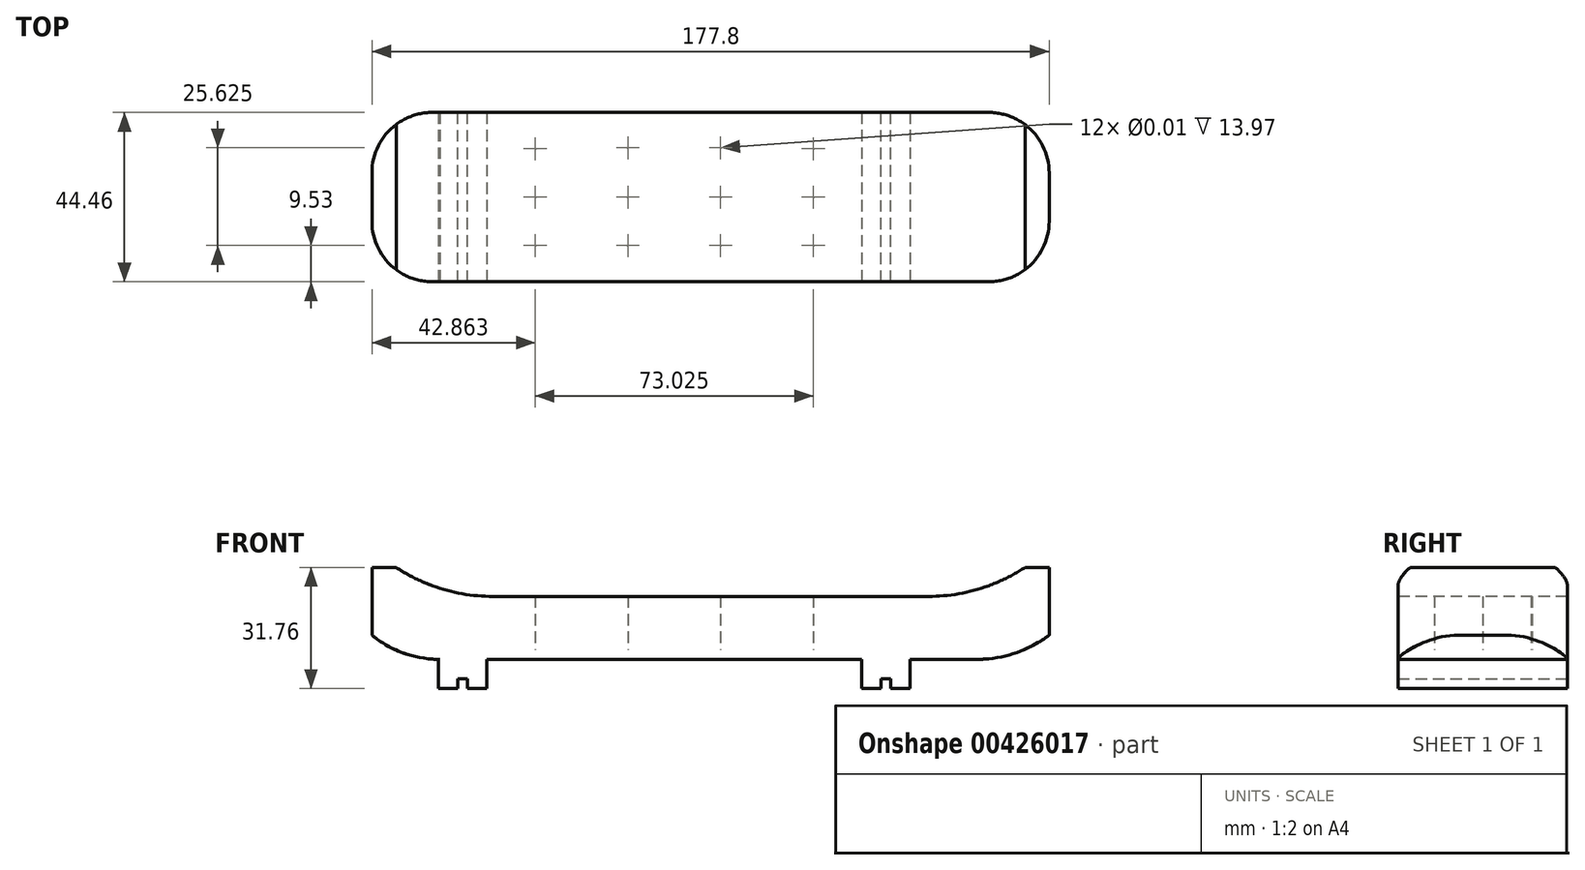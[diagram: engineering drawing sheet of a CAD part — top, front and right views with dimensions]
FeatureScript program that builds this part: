
annotation { "Feature Type Name" : "Feature", "Feature Type Description" : "" }
export const myFeature = defineFeature(function(context is Context, id is Id, definition is map)
    precondition{}
    {
        {
            var Q0;
            Q0=qCreatedBy(makeId("Front.planeOp"),FACE);
            var sketch = newSketch(context, id + "F0", { "sketchPlane" : qUnion([Q0])});
            skLineSegment(sketch, "E0.bottom", {"start": v(-88.9, -15.88) * mm, "end": v(88.9, -15.88) * mm});
            skLineSegment(sketch, "E0.top", {"start": v(-88.9, 15.88) * mm, "end": v(88.9, 15.88) * mm});
            skLineSegment(sketch, "E0.left", {"start": v(-88.9, -15.88) * mm, "end": v(-88.9, 15.88) * mm});
            skLineSegment(sketch, "E0.right", {"start": v(88.9, -15.88) * mm, "end": v(88.9, 15.88) * mm});
            skLineSegment(sketch, "E1", {"start": v(-88.9, 15.88) * mm, "end": v(88.9, -15.88) * mm, "construction": true});
            skPoint(sketch, "E2", {"position": v(0, 0) * mm});
            skSolve(sketch);
        }
        {
            var Q0;
            Q0=makeQuery(id+"F0.imprint","IMPRINT",FACE,{"disambiguationData":[TD([[makeQuery(id+"F0.imprint","IMPRINT",EDGE,{"derivedFrom":sQuery(id+"F0.wireOp",EDGE,"E0.bottom")}),1.0]])]});
            extrude(context, id + "F12", {"entities" : qUnion([Q0]), "endBound" : BoundingType.SYMMETRIC, "depth" : 44.45 * mm});
        }
        {
            var Q0;
            Q0=qCreatedBy(makeId("Front.planeOp"),FACE);
            var sketch = newSketch(context, id + "F1", { "sketchPlane" : qUnion([Q0])});
            skLineSegment(sketch, "E3.0", {"start": v(-88.9, -15.88) * mm, "end": v(88.9, -15.88) * mm, "construction": true});
            skLineSegment(sketch, "E4.bottom", {"start": v(-66.36, -15.88) * mm, "end": v(-63.82, -15.88) * mm});
            skLineSegment(sketch, "E4.top", {"start": v(-66.36, -13.34) * mm, "end": v(-63.82, -13.34) * mm});
            skLineSegment(sketch, "E4.left", {"start": v(-66.36, -15.88) * mm, "end": v(-66.36, -13.34) * mm});
            skLineSegment(sketch, "E4.right", {"start": v(-63.82, -15.88) * mm, "end": v(-63.82, -13.34) * mm});
            skLineSegment(sketch, "E5.bottom", {"start": v(44.77, -15.88) * mm, "end": v(47.3, -15.88) * mm});
            skLineSegment(sketch, "E5.top", {"start": v(44.77, -13.34) * mm, "end": v(47.3, -13.34) * mm});
            skLineSegment(sketch, "E5.left", {"start": v(44.77, -15.88) * mm, "end": v(44.77, -13.34) * mm});
            skLineSegment(sketch, "E5.right", {"start": v(47.3, -15.88) * mm, "end": v(47.3, -13.34) * mm});
            skPoint(sketch, "E6", {"position": v(-65.09, -15.88) * mm});
            skPoint(sketch, "E7", {"position": v(46.04, -15.88) * mm});
            skSolve(sketch);
        }
        {
            var Q0;
            Q0=qSketchRegion(id+"F1",true);
            extrude(context, id + "F2", {"entities" : qUnion([Q0]), "operationType" : NewBodyOperationType.REMOVE, "endBound" : BoundingType.UP_TO_NEXT, "depth" : 50.8 * mm, "hasSecondDirection" : true, "secondDirectionBound" : SecondDirectionBoundingType.UP_TO_NEXT, "secondDirectionOppositeDirection" : true, "secondDirectionDepth" : 25.4 * mm});
        }
        {
            var Q0;
            Q0=makeQuery(id+"F12.opExtrude","CAP_FACE",FACE,{"disambiguationData":[OSD([sQuery(id+"F0.wireOp",EDGE,"E0.bottom"),sQuery(id+"F0.wireOp",EDGE,"E0.top"),sQuery(id+"F0.wireOp",EDGE,"E0.left"),sQuery(id+"F0.wireOp",EDGE,"E0.right")])],"isStart":false});
            var sketch = newSketch(context, id + "F3", { "sketchPlane" : qUnion([Q0])});
            skLineSegment(sketch, "E8.bottom", {"start": v(-88.9, -15.88) * mm, "end": v(-71.44, -15.88) * mm});
            skLineSegment(sketch, "E8.top", {"start": v(-88.9, -8.26) * mm, "end": v(-71.44, -8.26) * mm});
            skLineSegment(sketch, "E8.left", {"start": v(-88.9, -15.88) * mm, "end": v(-88.9, -8.26) * mm});
            skLineSegment(sketch, "E8.right", {"start": v(-71.44, -15.88) * mm, "end": v(-71.44, -8.26) * mm});
            skLineSegment(sketch, "E9.bottom", {"start": v(-58.74, -15.88) * mm, "end": v(39.69, -15.88) * mm});
            skLineSegment(sketch, "E9.top", {"start": v(-58.74, -8.26) * mm, "end": v(39.69, -8.26) * mm});
            skLineSegment(sketch, "E9.left", {"start": v(-58.74, -15.88) * mm, "end": v(-58.74, -8.26) * mm});
            skLineSegment(sketch, "E9.right", {"start": v(39.69, -15.88) * mm, "end": v(39.69, -8.26) * mm});
            skLineSegment(sketch, "E10.bottom", {"start": v(88.9, -15.88) * mm, "end": v(52.39, -15.88) * mm});
            skLineSegment(sketch, "E10.top", {"start": v(88.9, -8.26) * mm, "end": v(52.39, -8.26) * mm});
            skLineSegment(sketch, "E10.left", {"start": v(88.9, -15.88) * mm, "end": v(88.9, -8.26) * mm});
            skLineSegment(sketch, "E10.right", {"start": v(52.39, -15.88) * mm, "end": v(52.39, -8.26) * mm});
            skLineSegment(sketch, "E11", {"start": v(39.69, -8.26) * mm, "end": v(52.39, -8.26) * mm, "construction": true});
            skPoint(sketch, "E12", {"position": v(46.04, -8.26) * mm});
            skPoint(sketch, "E13", {"position": v(46.04, -13.34) * mm});
            skLineSegment(sketch, "E14", {"start": v(-71.44, -8.26) * mm, "end": v(-58.74, -8.26) * mm, "construction": true});
            skPoint(sketch, "E15", {"position": v(-65.09, -8.26) * mm});
            skPoint(sketch, "E16", {"position": v(-65.09, -13.34) * mm});
            skSolve(sketch);
        }
        {
            var Q0;
            Q0=makeQuery(id+"F3.imprint","IMPRINT",FACE,{"disambiguationData":[TD([[makeQuery(id+"F3.imprint","IMPRINT",EDGE,{"derivedFrom":sQuery(id+"F3.wireOp",EDGE,"E8.bottom")}),1.0]])]});
            var Q1;
            Q1=makeQuery(id+"F3.imprint","IMPRINT",FACE,{"disambiguationData":[TD([[makeQuery(id+"F3.imprint","IMPRINT",EDGE,{"derivedFrom":sQuery(id+"F3.wireOp",EDGE,"E9.bottom")}),1.0]])]});
            var Q2;
            Q2=makeQuery(id+"F3.imprint","IMPRINT",FACE,{"disambiguationData":[TD([[makeQuery(id+"F3.imprint","IMPRINT",EDGE,{"derivedFrom":sQuery(id+"F3.wireOp",EDGE,"E10.bottom")}),1.0]])]});
            extrude(context, id + "F4", {"entities" : qUnion([Q0, Q1, Q2]), "operationType" : NewBodyOperationType.REMOVE, "endBound" : BoundingType.THROUGH_ALL, "oppositeDirection" : true, "depth" : 25.4 * mm});
        }
        {
            var Q0;
            Q0=makeQuery(id+"F12.opExtrude","CAP_FACE",FACE,{"disambiguationData":[OSD([sQuery(id+"F0.wireOp",EDGE,"E0.bottom"),sQuery(id+"F0.wireOp",EDGE,"E0.top"),sQuery(id+"F0.wireOp",EDGE,"E0.left"),sQuery(id+"F0.wireOp",EDGE,"E0.right")])],"isStart":false});
            var sketch = newSketch(context, id + "F5", { "sketchPlane" : qUnion([Q0])});
            skArc(sketch, "E17", {"start": v(-88.9, -1.9) * mm, "mid": v(-80.56, -6.62) * mm, "end": v(-71.12, -8.26) * mm});
            skLineSegment(sketch, "E18", {"start": v(-71.12, -8.26) * mm, "end": v(-88.9, -8.26) * mm});
            skLineSegment(sketch, "E19", {"start": v(-88.9, -8.26) * mm, "end": v(-88.9, -1.9) * mm});
            skArc(sketch, "E20", {"start": v(-82.55, 15.87) * mm, "mid": v(-70.4, 10.2) * mm, "end": v(-57.15, 8.25) * mm});
            skLineSegment(sketch, "E21", {"start": v(-57.15, 8.26) * mm, "end": v(57.15, 8.26) * mm});
            skArc(sketch, "E22", {"start": v(57.15, 8.26) * mm, "mid": v(70.4, 10.2) * mm, "end": v(82.55, 15.88) * mm});
            skLineSegment(sketch, "E23", {"start": v(-82.55, 15.87) * mm, "end": v(82.55, 15.88) * mm});
            skArc(sketch, "E24", {"start": v(69.85, -8.26) * mm, "mid": v(79.9, -6.63) * mm, "end": v(88.9, -1.9) * mm});
            skLineSegment(sketch, "E25", {"start": v(88.9, -1.9) * mm, "end": v(88.9, -8.26) * mm});
            skLineSegment(sketch, "E26", {"start": v(88.9, -8.26) * mm, "end": v(69.85, -8.26) * mm});
            skSolve(sketch);
        }
        {
            var Q0;
            Q0=makeQuery(id+"F5.imprint","IMPRINT",FACE,{"disambiguationData":[TD([[makeQuery(id+"F5.imprint","IMPRINT",EDGE,{"derivedFrom":sQuery(id+"F5.wireOp",EDGE,"E20")}),1.0]])]});
            var Q1;
            Q1=makeQuery(id+"F5.imprint","IMPRINT",FACE,{"disambiguationData":[TD([[makeQuery(id+"F5.imprint","IMPRINT",EDGE,{"derivedFrom":sQuery(id+"F5.wireOp",EDGE,"E17")}),-1.0]])]});
            var Q2;
            Q2=makeQuery(id+"F5.imprint","IMPRINT",FACE,{"disambiguationData":[TD([[makeQuery(id+"F5.imprint","IMPRINT",EDGE,{"derivedFrom":sQuery(id+"F5.wireOp",EDGE,"E24")}),-1.0]])]});
            extrude(context, id + "F6", {"entities" : qUnion([Q0, Q1, Q2]), "operationType" : NewBodyOperationType.REMOVE, "endBound" : BoundingType.THROUGH_ALL, "oppositeDirection" : true, "depth" : 25.4 * mm});
        }
        {
            var Q0;
            Q0=makeQuery(id+"F12.opExtrude","CAP_EDGE",EDGE,{"disambiguationData":[OSD([sQuery(id+"F0.wireOp",EDGE,"E0.left")])],"isStart":false});
            var Q1;
            Q1=makeQuery(id+"F12.opExtrude","CAP_EDGE",EDGE,{"disambiguationData":[OSD([sQuery(id+"F0.wireOp",EDGE,"E0.right")])],"isStart":false});
            var Q2;
            Q2=makeQuery(id+"F12.opExtrude","CAP_EDGE",EDGE,{"disambiguationData":[OSD([sQuery(id+"F0.wireOp",EDGE,"E0.right")])],"isStart":true});
            var Q3;
            Q3=makeQuery(id+"F12.opExtrude","CAP_EDGE",EDGE,{"disambiguationData":[OSD([sQuery(id+"F0.wireOp",EDGE,"E0.left")])],"isStart":true});
            fillet(context, id + "F7", {"entities" : qUnion([Q0, Q1, Q2, Q3]), "radius" : 15.88 * mm, "tangentPropagation" : true, "allowEdgeOverflow" : false});
        }
        {
            var Q0;
            Q0=makeQuery(id+"F4.boolean.opBoolean","COPY",FACE,{"derivedFrom":makeQuery(id+"F4.opExtrude","SWEPT_FACE",FACE,{"disambiguationData":[OSD([sQuery(id+"F3.wireOp",EDGE,"E9.top")])]})});
            var sketch = newSketch(context, id + "F8", { "sketchPlane" : qUnion([Q0])});
            skPoint(sketch, "E27", {"position": v(-46.04, 12.7) * mm});
            skPoint(sketch, "E28", {"position": v(-46.04, 0) * mm});
            skPoint(sketch, "E29", {"position": v(-46.04, -12.7) * mm});
            skPoint(sketch, "E30", {"position": v(26.99, 12.7) * mm});
            skPoint(sketch, "E31", {"position": v(26.99, 0) * mm});
            skPoint(sketch, "E32", {"position": v(26.99, -12.7) * mm});
            skLineSegment(sketch, "E33", {"start": v(2.65, 12.7) * mm, "end": v(26.99, 12.7) * mm, "construction": true});
            skLineSegment(sketch, "E34", {"start": v(-46.04, 12.7) * mm, "end": v(-21.7, 12.7) * mm, "construction": true});
            skLineSegment(sketch, "E35", {"start": v(-21.7, 12.7) * mm, "end": v(2.65, 12.7) * mm, "construction": true});
            skPoint(sketch, "E36", {"position": v(-21.7, 0) * mm});
            skPoint(sketch, "E37", {"position": v(2.65, 0) * mm});
            skPoint(sketch, "E38", {"position": v(-21.7, -12.92) * mm});
            skPoint(sketch, "E39", {"position": v(2.65, -12.92) * mm});
            skPoint(sketch, "E40", {"position": v(-21.7, 12.7) * mm});
            skPoint(sketch, "E41", {"position": v(2.65, 12.7) * mm});
            skSolve(sketch);
        }
        {
            var Q0;
            Q0=sQuery(id+"F8.wireOp",VERTEX,"E27");
            var Q1;
            Q1=sQuery(id+"F8.wireOp",VERTEX,"E28");
            var Q2;
            Q2=sQuery(id+"F8.wireOp",VERTEX,"E29");
            var Q3;
            Q3=sQuery(id+"F8.wireOp",VERTEX,"E32");
            var Q4;
            Q4=sQuery(id+"F8.wireOp",VERTEX,"E31");
            var Q5;
            Q5=sQuery(id+"F8.wireOp",VERTEX,"E30");
            var Q6;
            Q6=sQuery(id+"F8.wireOp",VERTEX,"E40");
            var Q7;
            Q7=sQuery(id+"F8.wireOp",VERTEX,"E41");
            var Q8;
            Q8=sQuery(id+"F8.wireOp",VERTEX,"E37");
            var Q9;
            Q9=sQuery(id+"F8.wireOp",VERTEX,"E36");
            var Q10;
            Q10=sQuery(id+"F8.wireOp",VERTEX,"E38");
            var Q11;
            Q11=sQuery(id+"F8.wireOp",VERTEX,"E39");
            var Q12;
            Q12=makeQuery(id+"F12.opExtrude","SWEPT_BODY",BODY,{"disambiguationData":[OSD([sQuery(id+"F0.wireOp",EDGE,"E0.bottom"),sQuery(id+"F0.wireOp",EDGE,"E0.top"),sQuery(id+"F0.wireOp",EDGE,"E0.left"),sQuery(id+"F0.wireOp",EDGE,"E0.right")])]});
            hole(context, id + "F9", {"style" : HoleStyle.SIMPLE, "endStyle" : HoleEndStyle.THROUGH, "standardTappedOrClearance" : lookupTablePath({ "standard" : "ANSI", "size" : "3/8 (0.38)", "type" : "Drilled" }), "standardBlindInLast" : lookupTablePath({ "standard" : "ANSI", "size" : "3/8", "type" : "Drilled" }), "holeDiameter" : 3 / 203.2 * mm, "isTappedThrough" : true, "tappedDepth" : 12.7 * mm, "tapClearance" : 3, "locations" : qUnion([Q0, Q1, Q2, Q3, Q4, Q5, Q6, Q7, Q8, Q9, Q10, Q11]), "scope" : qUnion([Q12])});
        }
        {
            var Q0;
            Q0=makeQuery(id+"F4.boolean.opBoolean","COPY",FACE,{"derivedFrom":makeQuery(id+"F4.opExtrude","SWEPT_FACE",FACE,{"disambiguationData":[OSD([sQuery(id+"F3.wireOp",EDGE,"E9.top")])]})});
            var sketch = newSketch(context, id + "F10", { "sketchPlane" : qUnion([Q0])});
            skLineSegment(sketch, "E42.bottom", {"start": v(-58.74, 22.23) * mm, "end": v(39.69, 22.23) * mm});
            skLineSegment(sketch, "E42.top", {"start": v(-58.74, -22.22) * mm, "end": v(39.69, -22.22) * mm});
            skLineSegment(sketch, "E42.left", {"start": v(-58.74, 22.23) * mm, "end": v(-58.74, -22.22) * mm});
            skLineSegment(sketch, "E42.right", {"start": v(39.69, 22.23) * mm, "end": v(39.69, -22.22) * mm});
            skSolve(sketch);
        }
        {
            var Q0;
            Q0 = qSketchRegion(id + "F10", true);
            extrude(context, id + "F11", {"entities" : qUnion([Q0]), "operationType" : NewBodyOperationType.ADD, "oppositeDirection" : true, "depth" : 2.54 * mm});
        }
    });
